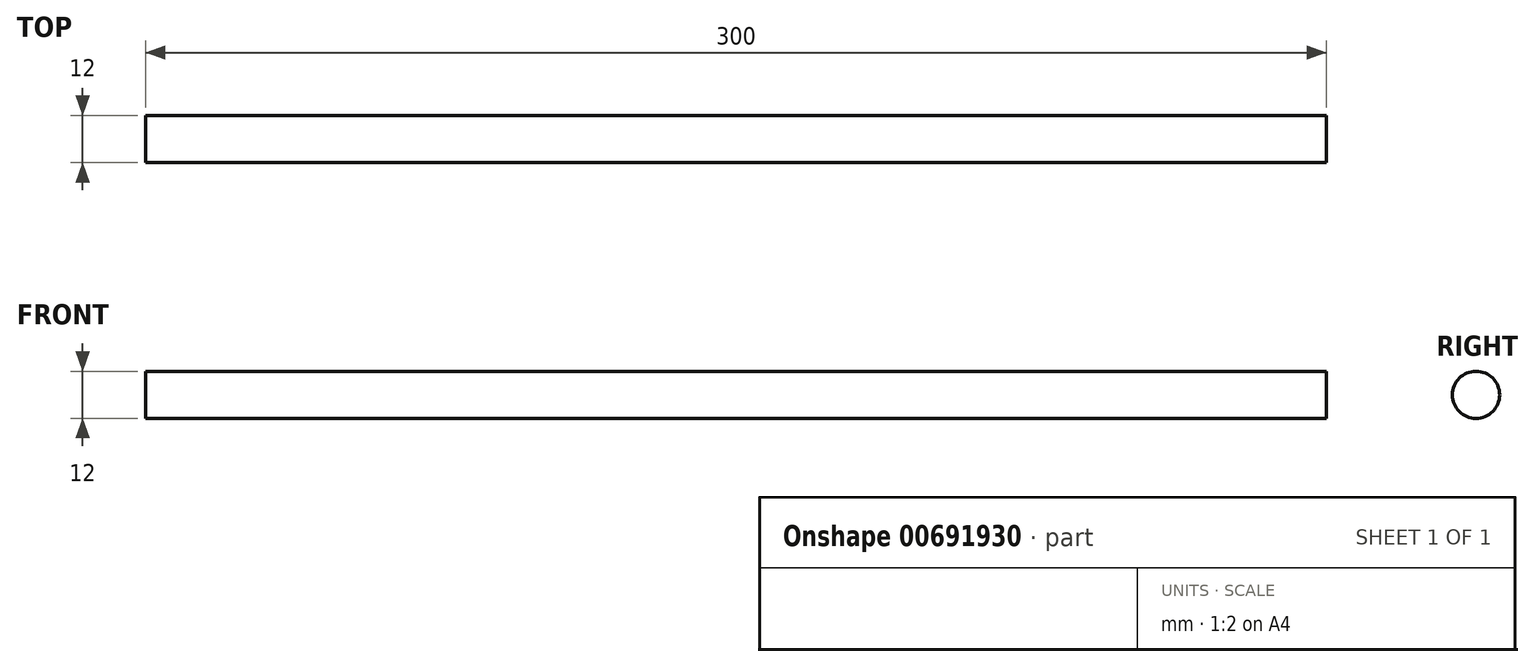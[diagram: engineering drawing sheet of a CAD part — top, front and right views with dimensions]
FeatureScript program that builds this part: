
annotation { "Feature Type Name" : "Feature", "Feature Type Description" : "" }
export const myFeature = defineFeature(function(context is Context, id is Id, definition is map)
    precondition{}
    {
        {
            var Q0;
            Q0=qCreatedBy(makeId("Top.planeOp"),FACE);
            var sketch = newSketch(context, id + "F0", { "sketchPlane" : qUnion([Q0])});
            skLineSegment(sketch, "E0.bottom", {"start": v(225, -5) * mm, "end": v(-75, -5) * mm});
            skLineSegment(sketch, "E0.top", {"start": v(225, 1) * mm, "end": v(-75, 1) * mm});
            skLineSegment(sketch, "E0.left", {"start": v(225, -5) * mm, "end": v(225, 1) * mm});
            skLineSegment(sketch, "E0.right", {"start": v(-75, -5) * mm, "end": v(-75, 1) * mm});
            skPoint(sketch, "E0.middle", {"position": v(0, 0) * mm});
            skSolve(sketch);
        }
        {
            var Q0;
            Q0=makeQuery(id+"F0.imprint","IMPRINT",FACE,{"disambiguationData":[TD([[makeQuery(id+"F0.imprint","IMPRINT",EDGE,{"derivedFrom":sQuery(id+"F0.wireOp",EDGE,"E0.bottom")}),-1.0]])]});
            var Q1;
            Q1=sQuery(id+"F0.wireOp",EDGE,"E0.bottom");
            revolve(context, id + "F1", {"entities" : qUnion([Q0]), "axis" : qUnion([Q1]), "revolveType" : RevolveType.FULL});
        }
    });
